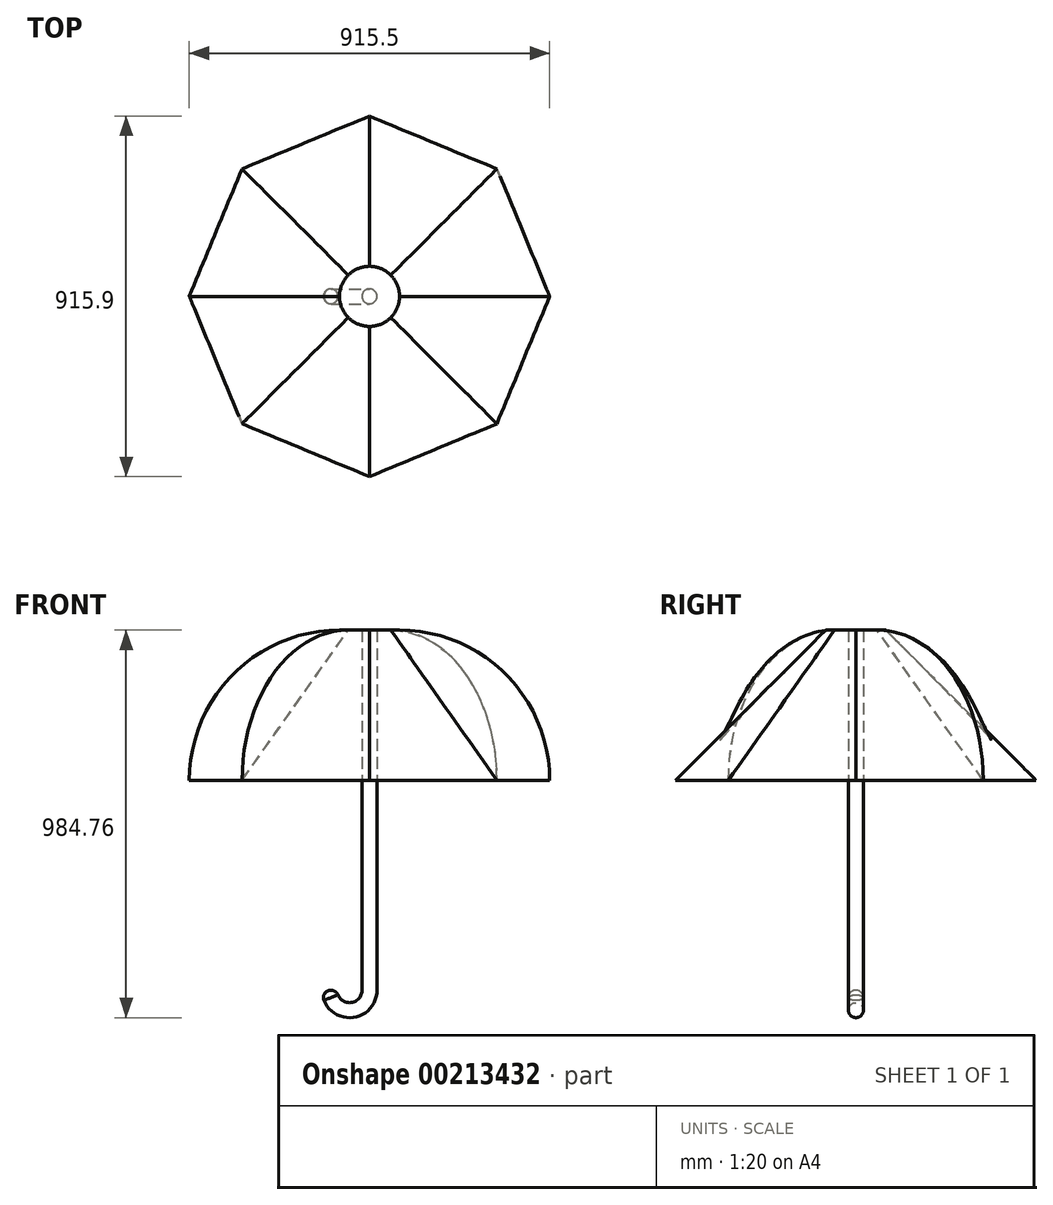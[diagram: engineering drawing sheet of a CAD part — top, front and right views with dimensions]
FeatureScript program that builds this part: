
annotation { "Feature Type Name" : "Feature", "Feature Type Description" : "" }
export const myFeature = defineFeature(function(context is Context, id is Id, definition is map)
    precondition{}
    {
        {
            var Q0;
            Q0=qCreatedBy(makeId("Top.planeOp"),FACE);
            cPlane(context, id + "F0", {"entities" : qUnion([Q0]), "cplaneType" : CPlaneType.OFFSET, "offset" : 381 * mm, "width" : 152.4 * mm, "height" : 152.4 * mm});
        }
        {
            var Q0;
            Q0=qCreatedBy(id+"F0.planeOp",FACE);
            var sketch = newSketch(context, id + "F1", { "sketchPlane" : qUnion([Q0])});
            skCircle(sketch, "E0", {"center": v(0, 0) * mm, "radius": 76.2 * mm});
            skLineSegment(sketch, "E1", {"start": v(0, 76.2) * mm, "end": v(0, -76.2) * mm, "construction": true});
            skLineSegment(sketch, "E2.1.0", {"start": v(53.88, 53.88) * mm, "end": v(-53.88, -53.88) * mm, "construction": true});
            skLineSegment(sketch, "E2.2.0", {"start": v(76.2, 0) * mm, "end": v(-76.2, 0) * mm, "construction": true});
            skLineSegment(sketch, "E2.3.0", {"start": v(53.88, -53.88) * mm, "end": v(-53.88, 53.88) * mm, "construction": true});
            skLineSegment(sketch, "E2.anchor1", {"start": v(0, 0) * mm, "end": v(0, -76.2) * mm, "construction": true});
            skLineSegment(sketch, "E2.anchor2", {"start": v(0, 0) * mm, "end": v(-53.88, 53.88) * mm, "construction": true});
            skSolve(sketch);
        }
        {
            var Q0;
            Q0=qCreatedBy(makeId("Front.planeOp"),FACE);
            var sketch = newSketch(context, id + "F2", { "sketchPlane" : qUnion([Q0])});
            skLineSegment(sketch, "E3", {"start": v(0, 0) * mm, "end": v(0, 381) * mm, "construction": true});
            skSolve(sketch);
        }
        {
            var Q0;
            Q0=qCreatedBy(makeId("Top.planeOp"),FACE);
            var sketch = newSketch(context, id + "F3", { "sketchPlane" : qUnion([Q0])});
            skCircle(sketch, "E4.cCircle", {"center": v(0, 0) * mm, "radius": 422.4 * mm, "construction": true});
            skLineSegment(sketch, "E4.0", {"start": v(323.29, 323.29) * mm, "end": v(457.2, 0) * mm});
            skLineSegment(sketch, "E4.1", {"start": v(457.2, 0) * mm, "end": v(323.29, -323.29) * mm});
            skLineSegment(sketch, "E4.2", {"start": v(323.29, -323.29) * mm, "end": v(0, -457.2) * mm});
            skLineSegment(sketch, "E4.3", {"start": v(0, -457.2) * mm, "end": v(-323.29, -323.29) * mm});
            skLineSegment(sketch, "E4.4", {"start": v(-323.29, -323.29) * mm, "end": v(-457.2, 0) * mm});
            skLineSegment(sketch, "E4.5", {"start": v(-457.2, 0) * mm, "end": v(-323.29, 323.29) * mm});
            skLineSegment(sketch, "E4.6", {"start": v(-323.29, 323.29) * mm, "end": v(0, 457.2) * mm});
            skLineSegment(sketch, "E4.7", {"start": v(0, 457.2) * mm, "end": v(323.29, 323.29) * mm});
            skPoint(sketch, "E4.0.midPoint", {"position": v(390.24, 161.64) * mm});
            skLineSegment(sketch, "E5", {"start": v(0, 457.2) * mm, "end": v(0, -457.2) * mm, "construction": true});
            skSolve(sketch);
        }
        {
            var Q0;
            Q0=qCreatedBy(makeId("Front.planeOp"),FACE);
            var sketch = newSketch(context, id + "F4", { "sketchPlane" : qUnion([Q0])});
            skArc(sketch, "E6", {"start": v(457.2, 0) * mm, "mid": v(345.6, 269.4) * mm, "end": v(76.2, 381) * mm});
            skArc(sketch, "E7.MirrorCS", {"start": v(-457.2, 0) * mm, "mid": v(-345.6, 269.4) * mm, "end": v(-76.2, 381) * mm});
            skSolve(sketch);
        }
        {
            var Q0;
            Q0=qCreatedBy(makeId("Front.planeOp"),FACE);
            var Q1;
            Q1=sQuery(id+"F2.wireOp",EDGE,"E3");
            cPlane(context, id + "F5", {"entities" : qUnion([Q0, Q1]), "cplaneType" : CPlaneType.LINE_ANGLE, "offset" : 25.4 * mm, "angle" : 45 * degree, "width" : 152.4 * mm, "height" : 152.4 * mm});
        }
        {
            var Q0;
            Q0=qCreatedBy(id+"F5.planeOp",FACE);
            var sketch = newSketch(context, id + "F6", { "sketchPlane" : qUnion([Q0])});
            skArc(sketch, "E8", {"start": v(-76.2, 381) * mm, "mid": v(-345.6, 269.4) * mm, "end": v(-457.2, 0) * mm});
            skArc(sketch, "E9.MirrorCS", {"start": v(76.2, 381) * mm, "mid": v(345.6, 269.4) * mm, "end": v(457.2, 0) * mm});
            skSolve(sketch);
        }
        {
            var Q0;
            Q0=makeQuery(id+"F3.imprint","IMPRINT",FACE,{"disambiguationData":[TD([[makeQuery(id+"F3.imprint","IMPRINT",EDGE,{"derivedFrom":sQuery(id+"F3.wireOp",EDGE,"E4.0")}),-1.0]])]});
            var Q1;
            Q1=makeQuery(id+"F1.imprint","IMPRINT",FACE,{"disambiguationData":[TD([[makeQuery(id+"F1.imprint","IMPRINT",EDGE,{"derivedFrom":sQuery(id+"F1.wireOp",EDGE,"E0")}),1.0]])]});
            var Q2;
            Q2=sQuery(id+"F4.wireOp",EDGE,"E6");
            var Q3;
            Q3=sQuery(id+"FwEUsNg9eqqxYRy_0.1.F6.wireOp",EDGE,"E9.MirrorCS");
            var Q4;
            Q4=sQuery(id+"FwEUsNg9eqqxYRy_0.1.F4.wireOp",EDGE,"E7.MirrorCS");
            var Q5;
            Q5=sQuery(id+"F6.wireOp",EDGE,"E9.MirrorCS");
            var Q6;
            Q6=sQuery(id+"F4.wireOp",EDGE,"E7.MirrorCS");
            var Q7;
            Q7=sQuery(id+"FwEUsNg9eqqxYRy_0.1.F6.wireOp",EDGE,"E8");
            var Q8;
            Q8=sQuery(id+"FwEUsNg9eqqxYRy_0.1.F4.wireOp",EDGE,"E6");
            var Q9;
            Q9=sQuery(id+"F6.wireOp",EDGE,"E8");
            loft(context, id + "F7", {"addGuides" : true, "sheetProfilesArray" : [{ "sheetProfileEntities" : qUnion([Q0]) }, { "sheetProfileEntities" : qUnion([Q1]) }], "guidesArray" : [{ "guideEntities" : qUnion([Q2]), "guideDerivativeType" : LoftGuideDerivativeType.DEFAULT, "guideDerivativeMagnitude" : 1 }, { "guideEntities" : qUnion([Q3]), "guideDerivativeType" : LoftGuideDerivativeType.DEFAULT, "guideDerivativeMagnitude" : 1 }, { "guideEntities" : qUnion([Q4]), "guideDerivativeType" : LoftGuideDerivativeType.DEFAULT, "guideDerivativeMagnitude" : 1 }, { "guideEntities" : qUnion([Q5]), "guideDerivativeType" : LoftGuideDerivativeType.DEFAULT, "guideDerivativeMagnitude" : 1 }, { "guideEntities" : qUnion([Q6]), "guideDerivativeType" : LoftGuideDerivativeType.DEFAULT, "guideDerivativeMagnitude" : 1 }, { "guideEntities" : qUnion([Q7]), "guideDerivativeType" : LoftGuideDerivativeType.DEFAULT, "guideDerivativeMagnitude" : 1 }, { "guideEntities" : qUnion([Q8]), "guideDerivativeType" : LoftGuideDerivativeType.DEFAULT, "guideDerivativeMagnitude" : 1 }, { "guideEntities" : qUnion([Q9]), "guideDerivativeType" : LoftGuideDerivativeType.DEFAULT, "guideDerivativeMagnitude" : 1 }]});
        }
        {
            var Q0;
            Q0=makeQuery(id+"F7.opLoft","CAP_FACE",FACE,{"disambiguationData":[OSD([makeQuery(id+"F3.imprint","IMPRINT",FACE,{"disambiguationData":[TD([[makeQuery(id+"F3.imprint","IMPRINT",EDGE,{"derivedFrom":sQuery(id+"F3.wireOp",EDGE,"E4.0")}),-1.0]])]})])],"isStart":true});
            shell(context, id + "F8", {"entities" : qUnion([Q0]), "thickness" : 0.5 * mm, "oppositeDirection" : true});
        }
        {
            var Q0;
            Q0=qCreatedBy(makeId("Front.planeOp"),FACE);
            var sketch = newSketch(context, id + "F9", { "sketchPlane" : qUnion([Q0])});
            skLineSegment(sketch, "E10", {"start": v(0, 381) * mm, "end": v(0, -533.4) * mm});
            skArc(sketch, "E11", {"start": v(-101.6, -533.4) * mm, "mid": v(-50.8, -584.2) * mm, "end": v(0, -533.4) * mm});
            skSolve(sketch);
        }
        {
            var Q0;
            Q0=qCreatedBy(id+"F0.planeOp",FACE);
            var sketch = newSketch(context, id + "F10", { "sketchPlane" : qUnion([Q0])});
            skCircle(sketch, "E12", {"center": v(0, 0) * mm, "radius": 19.05 * mm});
            skSolve(sketch);
        }
        {
            var Q0;
            Q0=makeQuery(id+"F10.imprint","IMPRINT",FACE,{"disambiguationData":[TD([[makeQuery(id+"F10.imprint","IMPRINT",EDGE,{"derivedFrom":sQuery(id+"F10.wireOp",EDGE,"E12")}),1.0]])]});
            var Q1;
            Q1=sQuery(id+"F9.wireOp",EDGE,"E10");
            var Q2;
            Q2=sQuery(id+"F9.wireOp",EDGE,"E11");
            sweep(context, id + "F11", {"profiles" : qUnion([Q0]), "path" : qUnion([Q1, Q2])});
        }
        {
            var Q0;
            Q0=makeQuery(id+"F11.opSweep","CAP_EDGE",EDGE,{"disambiguationData":[OSD([sQuery(id+"F9.wireOp",VERTEX,"E11.start"),sQuery(id+"F10.wireOp",EDGE,"E12")])],"isStart":false});
            fillet(context, id + "F12", {"entities" : qUnion([Q0]), "radius" : 19.05 * mm, "tangentPropagation" : true, "allowEdgeOverflow" : false});
        }
    });
